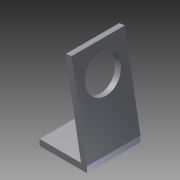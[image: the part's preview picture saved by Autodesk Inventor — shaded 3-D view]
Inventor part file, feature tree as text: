
AUTODESK INVENTOR PART (.ipt)
format: ipt  version: 2012 (Build 160160000, 160)  size: 90,112 bytes
history: native  units: in
note: dims shown in document units (in); Inventor stores cm internally (conversion verified against a paired STEP export)
features: extrude x2, sketch x2
ambient origin geometry x8: Origin, YZ Plane, XZ Plane, XY Plane, X Axis, Y Axis, Z Axis, Center Point
bodies: Solid1 (feature_tree)
feature tree (4):
  extrude  "Extrusion1"  Depth=1.0in
  extrude  "Extrusion2"  Depth=0.5497in
  sketch  "Sketch1"  dims[d0=0.125in d1=1.0in]
  sketch  "Sketch2"  dims[d3=0.125in d4=0.5497in d5=1.875in d6=1.125in d7=0.0in d8=0.75in d9=0.5625in d10=0.5625in d11=1.125in d12=0.0in]
